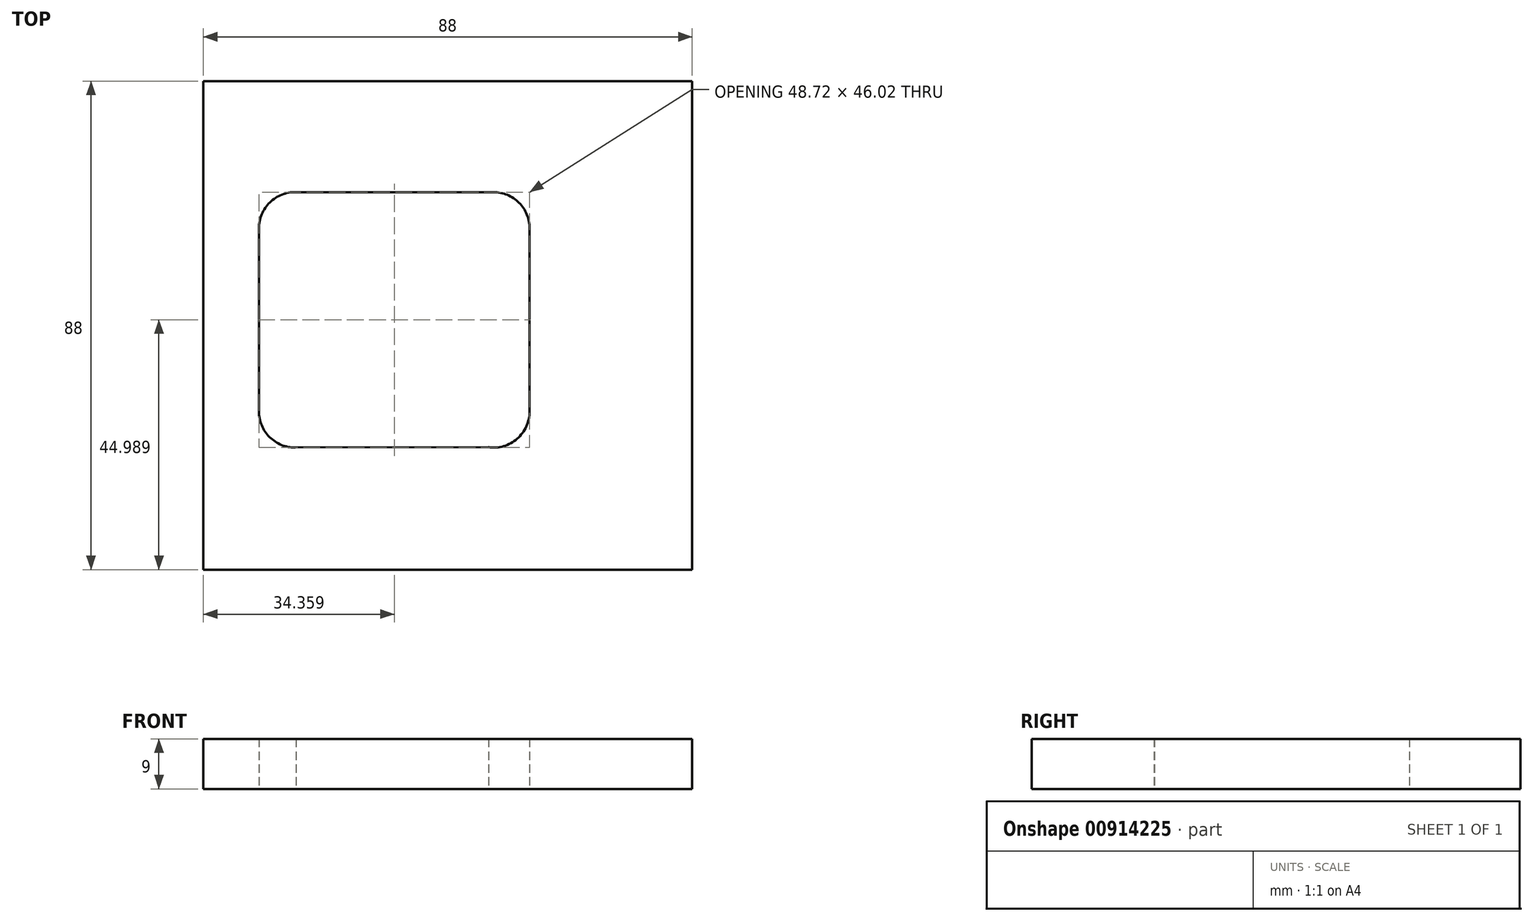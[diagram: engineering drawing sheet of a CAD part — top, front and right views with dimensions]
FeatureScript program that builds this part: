
annotation { "Feature Type Name" : "Feature", "Feature Type Description" : "" }
export const myFeature = defineFeature(function(context is Context, id is Id, definition is map)
    precondition{}
    {
        {
            var Q0;
            Q0=qCreatedBy(makeId("Top.planeOp"),FACE);
            var sketch = newSketch(context, id + "F0", { "sketchPlane" : qUnion([Q0])});
            skLineSegment(sketch, "E0.bottom", {"start": v(44, 44) * mm, "end": v(-44, 44) * mm});
            skLineSegment(sketch, "E0.top", {"start": v(44, -44) * mm, "end": v(-44, -44) * mm});
            skLineSegment(sketch, "E0.left", {"start": v(44, 44) * mm, "end": v(44, -44) * mm});
            skLineSegment(sketch, "E0.right", {"start": v(-44, 44) * mm, "end": v(-44, -44) * mm});
            skPoint(sketch, "E0.middle", {"position": v(0, 0) * mm});
            skLineSegment(sketch, "E1", {"start": v(-34, 57.89) * mm, "end": v(-34, 44) * mm, "construction": true});
            skArc(sketch, "E2", {"start": v(-27.34, 24) * mm, "mid": v(-32.04, 22.15) * mm, "end": v(-34, 17.5) * mm});
            skArc(sketch, "E3", {"start": v(14.72, 17.5) * mm, "mid": v(12.81, 22.1) * mm, "end": v(8.22, 24) * mm});
            skArc(sketch, "E4", {"start": v(-34, -15.52) * mm, "mid": v(-32.09, -20.13) * mm, "end": v(-27.48, -22.02) * mm});
            skArc(sketch, "E5", {"start": v(7.32, -21.96) * mm, "mid": v(12.49, -20.42) * mm, "end": v(14.72, -15.52) * mm});
            skLineSegment(sketch, "E6", {"start": v(-27.34, 24) * mm, "end": v(8.22, 24) * mm});
            skLineSegment(sketch, "E7", {"start": v(-34, 17.5) * mm, "end": v(-34, -15.52) * mm});
            skLineSegment(sketch, "E8", {"start": v(14.72, 17.5) * mm, "end": v(14.72, -15.52) * mm});
            skLineSegment(sketch, "E9", {"start": v(-27.5, -22.02) * mm, "end": v(9.14, -21.96) * mm});
            skSolve(sketch);
        }
        {
            var Q0;
            Q0=makeQuery(id+"F0.imprint","IMPRINT",FACE,{"disambiguationData":[TD([[makeQuery(id+"F0.imprint","IMPRINT",EDGE,{"derivedFrom":sQuery(id+"F0.wireOp",EDGE,"E0.bottom")}),1.0]])]});
            extrude(context, id + "F1", {"entities" : qUnion([Q0]), "depth" : 9 * mm, "offsetDistance" : 25 * mm});
        }
    });
